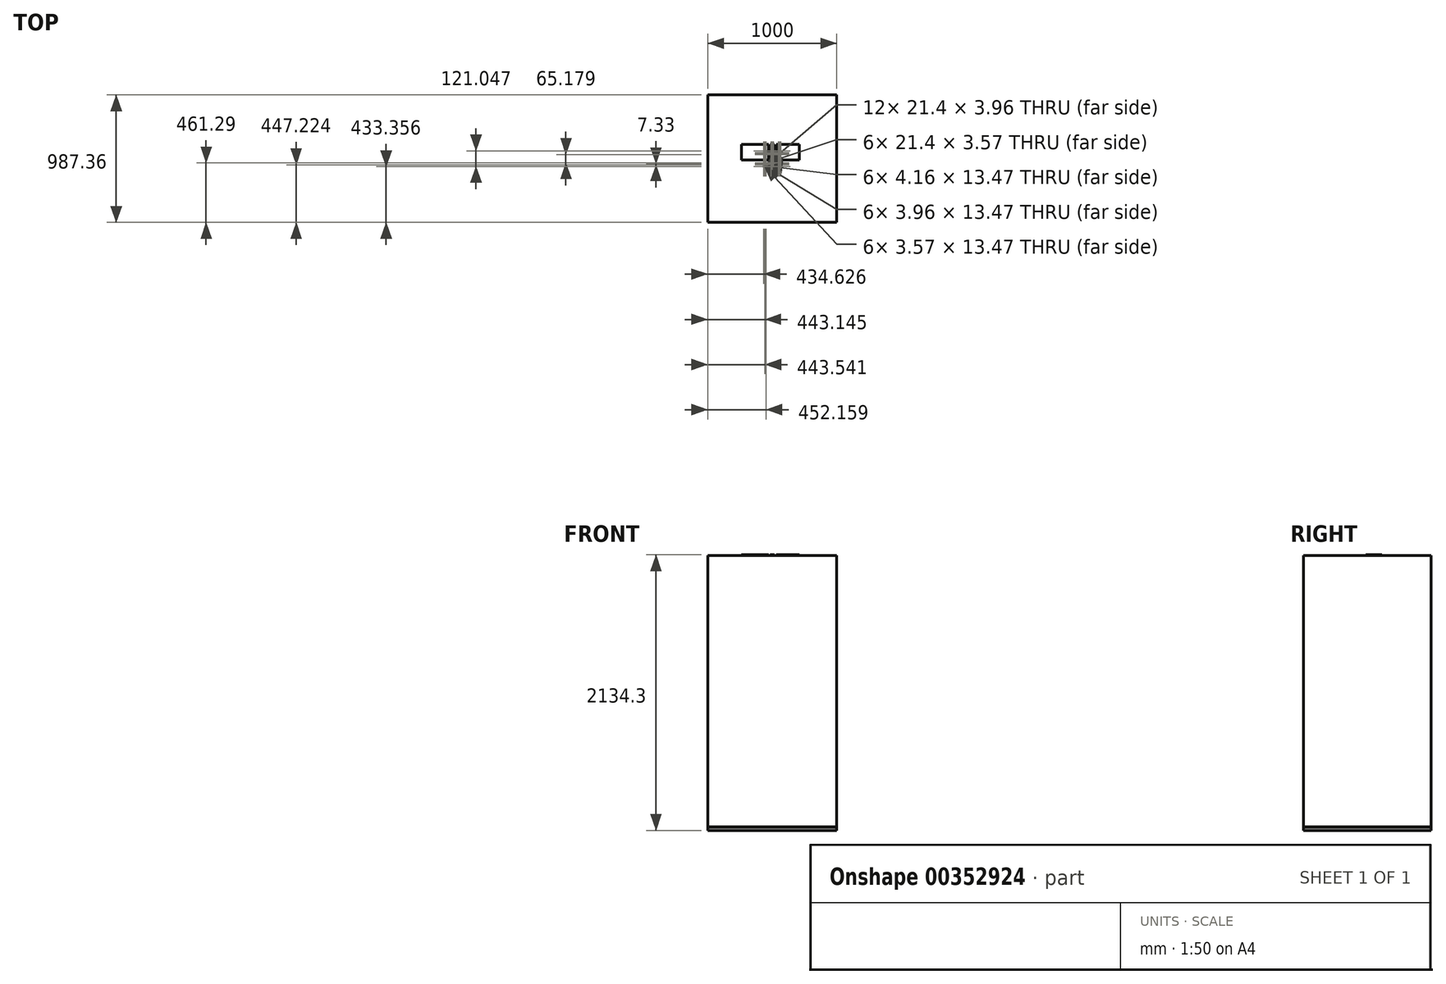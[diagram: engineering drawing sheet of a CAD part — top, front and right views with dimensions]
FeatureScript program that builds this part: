
annotation { "Feature Type Name" : "Feature", "Feature Type Description" : "" }
export const myFeature = defineFeature(function(context is Context, id is Id, definition is map)
    precondition{}
    {
        {
            var Q0;
            Q0=qCreatedBy(makeId("Top.planeOp"),FACE);
            var sketch = newSketch(context, id + "F0", { "sketchPlane" : qUnion([Q0])});
            skLineSegment(sketch, "E0.bottom", {"start": v(-500.4, 493.48) * mm, "end": v(499.6, 493.48) * mm});
            skLineSegment(sketch, "E0.top", {"start": v(-500.4, -493.88) * mm, "end": v(499.6, -493.88) * mm});
            skLineSegment(sketch, "E0.left", {"start": v(-500.4, 493.48) * mm, "end": v(-500.4, -493.88) * mm});
            skLineSegment(sketch, "E0.right", {"start": v(499.6, 493.48) * mm, "end": v(499.6, -493.88) * mm});
            skLineSegment(sketch, "E1.bottom", {"start": v(-441.4, 433.09) * mm, "end": v(443.42, 433.09) * mm});
            skLineSegment(sketch, "E1.top", {"start": v(-441.4, -436.3) * mm, "end": v(443.42, -436.3) * mm});
            skLineSegment(sketch, "E1.left", {"start": v(-441.4, 433.09) * mm, "end": v(-441.4, -436.3) * mm});
            skLineSegment(sketch, "E1.right", {"start": v(443.42, 433.09) * mm, "end": v(443.42, -436.3) * mm});
            skSolve(sketch);
        }
        {
            var Q0;
            Q0=makeQuery(id+"F0.imprint","IMPRINT",FACE,{"disambiguationData":[TD([[makeQuery(id+"F0.imprint","IMPRINT",EDGE,{"derivedFrom":sQuery(id+"F0.wireOp",EDGE,"E0.bottom")}),-1.0]])]});
            var Q1;
            Q1=makeQuery(id+"F0.imprint","IMPRINT",FACE,{"disambiguationData":[TD([[makeQuery(id+"F0.imprint","IMPRINT",EDGE,{"derivedFrom":sQuery(id+"F0.wireOp",EDGE,"E1.bottom")}),-1.0]])]});
            extrude(context, id + "F1", {"entities" : qUnion([Q0, Q1]), "depth" : 2100 * mm});
        }
        {
            var Q0;
            Q0=makeQuery(id+"F1.opExtrude","CAP_FACE",FACE,{"disambiguationData":[OSD([sQuery(id+"F0.wireOp",EDGE,"E0.bottom"),sQuery(id+"F0.wireOp",EDGE,"E0.top"),sQuery(id+"F0.wireOp",EDGE,"E0.left"),sQuery(id+"F0.wireOp",EDGE,"E0.right")])],"isStart":false});
            var sketch = newSketch(context, id + "F2", { "sketchPlane" : qUnion([Q0])});
            skLineSegment(sketch, "E2.bottom", {"start": v(-239.5, 111.47) * mm, "end": v(-29.32, 111.47) * mm});
            skLineSegment(sketch, "E2.top", {"start": v(-239.5, -10.2) * mm, "end": v(-29.32, -10.2) * mm});
            skLineSegment(sketch, "E2.left", {"start": v(-239.5, 111.47) * mm, "end": v(-239.5, -10.2) * mm});
            skLineSegment(sketch, "E2.right", {"start": v(-29.32, 111.47) * mm, "end": v(-29.32, -10.2) * mm});
            skLineSegment(sketch, "E3.bottom", {"start": v(-15.25, 111.47) * mm, "end": v(15.85, 111.47) * mm});
            skLineSegment(sketch, "E3.top", {"start": v(-15.25, -10.2) * mm, "end": v(15.85, -10.2) * mm});
            skLineSegment(sketch, "E3.left", {"start": v(-15.25, 111.47) * mm, "end": v(-15.25, -10.2) * mm});
            skLineSegment(sketch, "E3.right", {"start": v(15.85, 111.47) * mm, "end": v(15.85, -10.2) * mm});
            skLineSegment(sketch, "E4.bottom", {"start": v(30.7, 111.47) * mm, "end": v(210.08, 111.47) * mm});
            skLineSegment(sketch, "E4.top", {"start": v(30.7, -10.2) * mm, "end": v(210.08, -10.2) * mm});
            skLineSegment(sketch, "E4.left", {"start": v(30.7, 111.47) * mm, "end": v(30.7, -10.2) * mm});
            skLineSegment(sketch, "E4.right", {"start": v(210.08, 111.47) * mm, "end": v(210.08, -10.2) * mm});
            skSolve(sketch);
        }
        {
            var Q0;
            Q0=makeQuery(id+"F2.imprint","IMPRINT",FACE,{"disambiguationData":[TD([[makeQuery(id+"F2.imprint","IMPRINT",EDGE,{"derivedFrom":sQuery(id+"F2.wireOp",EDGE,"E3.bottom")}),-1.0]])]});
            var Q1;
            Q1=makeQuery(id+"F2.imprint","IMPRINT",FACE,{"disambiguationData":[TD([[makeQuery(id+"F2.imprint","IMPRINT",EDGE,{"derivedFrom":sQuery(id+"F2.wireOp",EDGE,"E4.bottom")}),-1.0]])]});
            var Q2;
            Q2=makeQuery(id+"F2.imprint","IMPRINT",FACE,{"disambiguationData":[TD([[makeQuery(id+"F2.imprint","IMPRINT",EDGE,{"derivedFrom":sQuery(id+"F2.wireOp",EDGE,"E2.bottom")}),-1.0]])]});
            extrude(context, id + "F3", {"entities" : qUnion([Q0, Q1, Q2]), "operationType" : NewBodyOperationType.ADD, "depth" : 5.8 * mm});
        }
        {
            var Q0;
            Q0=makeQuery(id+"F1.opExtrude","CAP_FACE",FACE,{"disambiguationData":[OSD([sQuery(id+"F0.wireOp",EDGE,"E0.bottom"),sQuery(id+"F0.wireOp",EDGE,"E0.top"),sQuery(id+"F0.wireOp",EDGE,"E0.left"),sQuery(id+"F0.wireOp",EDGE,"E0.right")])],"isStart":true});
            var sketch = newSketch(context, id + "F4", { "sketchPlane" : qUnion([Q0])});
            skLineSegment(sketch, "E5.bottom", {"start": v(-67.56, 67.26) * mm, "end": v(-64, 67.26) * mm});
            skLineSegment(sketch, "E5.top", {"start": v(-67.56, 53.79) * mm, "end": v(-64, 53.79) * mm});
            skLineSegment(sketch, "E5.left", {"start": v(-67.56, 67.26) * mm, "end": v(-67.56, 53.79) * mm});
            skLineSegment(sketch, "E5.right", {"start": v(-64, 67.26) * mm, "end": v(-64, 53.79) * mm});
            skLineSegment(sketch, "E6.bottom", {"start": v(-59.24, 67.26) * mm, "end": v(-55.27, 67.26) * mm});
            skLineSegment(sketch, "E6.top", {"start": v(-59.24, 53.79) * mm, "end": v(-55.27, 53.79) * mm});
            skLineSegment(sketch, "E6.left", {"start": v(-59.24, 67.26) * mm, "end": v(-59.24, 53.79) * mm});
            skLineSegment(sketch, "E6.right", {"start": v(-55.27, 67.26) * mm, "end": v(-55.27, 53.79) * mm});
            skLineSegment(sketch, "E7.bottom", {"start": v(-50.32, 67.26) * mm, "end": v(-46.16, 67.26) * mm});
            skLineSegment(sketch, "E7.top", {"start": v(-50.32, 53.79) * mm, "end": v(-46.16, 53.79) * mm});
            skLineSegment(sketch, "E7.left", {"start": v(-50.32, 67.26) * mm, "end": v(-50.32, 53.79) * mm});
            skLineSegment(sketch, "E7.right", {"start": v(-46.16, 67.26) * mm, "end": v(-46.16, 53.79) * mm});
            skLineSegment(sketch, "E8.1.0.0", {"start": v(-7.23, 66.87) * mm, "end": v(-7.23, 53.4) * mm});
            skLineSegment(sketch, "E8.1.0.1", {"start": v(1.48, 66.87) * mm, "end": v(1.48, 53.4) * mm});
            skLineSegment(sketch, "E8.1.0.2", {"start": v(-2.48, 66.87) * mm, "end": v(-2.48, 53.4) * mm});
            skLineSegment(sketch, "E8.1.0.3", {"start": v(6.44, 66.87) * mm, "end": v(6.44, 53.4) * mm});
            skLineSegment(sketch, "E8.1.0.4", {"start": v(10.6, 66.87) * mm, "end": v(10.6, 53.4) * mm});
            skLineSegment(sketch, "E8.1.0.5", {"start": v(-10.8, 66.87) * mm, "end": v(-7.23, 66.87) * mm});
            skLineSegment(sketch, "E8.1.0.6", {"start": v(-10.8, 53.4) * mm, "end": v(-7.23, 53.4) * mm});
            skLineSegment(sketch, "E8.1.0.7", {"start": v(-10.8, 66.87) * mm, "end": v(-10.8, 53.4) * mm});
            skLineSegment(sketch, "E8.1.0.8", {"start": v(-2.48, 66.87) * mm, "end": v(1.48, 66.87) * mm});
            skLineSegment(sketch, "E8.1.0.9", {"start": v(6.44, 66.87) * mm, "end": v(10.6, 66.87) * mm});
            skLineSegment(sketch, "E8.1.0.10", {"start": v(-2.48, 53.4) * mm, "end": v(1.48, 53.4) * mm});
            skLineSegment(sketch, "E8.1.0.11", {"start": v(6.44, 53.4) * mm, "end": v(10.6, 53.4) * mm});
            skLineSegment(sketch, "E8.2.0.0", {"start": v(49.52, 66.48) * mm, "end": v(49.52, 53.01) * mm});
            skLineSegment(sketch, "E8.2.0.1", {"start": v(58.24, 66.48) * mm, "end": v(58.24, 53.01) * mm});
            skLineSegment(sketch, "E8.2.0.2", {"start": v(54.28, 66.48) * mm, "end": v(54.28, 53.01) * mm});
            skLineSegment(sketch, "E8.2.0.3", {"start": v(63.2, 66.48) * mm, "end": v(63.2, 53.01) * mm});
            skLineSegment(sketch, "E8.2.0.4", {"start": v(67.35, 66.48) * mm, "end": v(67.35, 53.01) * mm});
            skLineSegment(sketch, "E8.2.0.5", {"start": v(45.96, 66.48) * mm, "end": v(49.52, 66.48) * mm});
            skLineSegment(sketch, "E8.2.0.6", {"start": v(45.96, 53.01) * mm, "end": v(49.52, 53.01) * mm});
            skLineSegment(sketch, "E8.2.0.7", {"start": v(45.96, 66.48) * mm, "end": v(45.96, 53.01) * mm});
            skLineSegment(sketch, "E8.2.0.8", {"start": v(54.28, 66.48) * mm, "end": v(58.24, 66.48) * mm});
            skLineSegment(sketch, "E8.2.0.9", {"start": v(63.2, 66.48) * mm, "end": v(67.35, 66.48) * mm});
            skLineSegment(sketch, "E8.2.0.10", {"start": v(54.28, 53.01) * mm, "end": v(58.24, 53.01) * mm});
            skLineSegment(sketch, "E8.2.0.11", {"start": v(63.2, 53.01) * mm, "end": v(67.35, 53.01) * mm});
            skLineSegment(sketch, "E9.MirrorCS", {"start": v(-59.24, -53.79) * mm, "end": v(-55.27, -53.79) * mm});
            skLineSegment(sketch, "E10.MirrorCS", {"start": v(-67.56, -53.79) * mm, "end": v(-64, -53.79) * mm});
            skLineSegment(sketch, "E11.MirrorCS", {"start": v(-50.32, -53.79) * mm, "end": v(-46.16, -53.79) * mm});
            skLineSegment(sketch, "E12.MirrorCS", {"start": v(54.28, -53.01) * mm, "end": v(58.24, -53.01) * mm});
            skLineSegment(sketch, "E13.MirrorCS", {"start": v(-10.8, -66.87) * mm, "end": v(-7.23, -66.87) * mm});
            skLineSegment(sketch, "E14.MirrorCS", {"start": v(-50.32, -67.26) * mm, "end": v(-46.16, -67.26) * mm});
            skLineSegment(sketch, "E15.MirrorCS", {"start": v(-10.8, -53.4) * mm, "end": v(-7.23, -53.4) * mm});
            skLineSegment(sketch, "E16.MirrorCS", {"start": v(54.28, -66.48) * mm, "end": v(58.24, -66.48) * mm});
            skLineSegment(sketch, "E17.MirrorCS", {"start": v(-67.56, -67.26) * mm, "end": v(-64, -67.26) * mm});
            skLineSegment(sketch, "E18.MirrorCS", {"start": v(-59.24, -67.26) * mm, "end": v(-55.27, -67.26) * mm});
            skLineSegment(sketch, "E19.MirrorCS", {"start": v(45.96, -53.01) * mm, "end": v(49.52, -53.01) * mm});
            skLineSegment(sketch, "E20.MirrorCS", {"start": v(6.44, -66.87) * mm, "end": v(10.6, -66.87) * mm});
            skLineSegment(sketch, "E21.MirrorCS", {"start": v(45.96, -66.48) * mm, "end": v(49.52, -66.48) * mm});
            skLineSegment(sketch, "E22.MirrorCS", {"start": v(-2.48, -66.87) * mm, "end": v(1.48, -66.87) * mm});
            skLineSegment(sketch, "E23.MirrorCS", {"start": v(-2.48, -53.4) * mm, "end": v(1.48, -53.4) * mm});
            skLineSegment(sketch, "E24.MirrorCS", {"start": v(6.44, -53.4) * mm, "end": v(10.6, -53.4) * mm});
            skLineSegment(sketch, "E25.MirrorCS", {"start": v(58.24, -66.48) * mm, "end": v(58.24, -53.01) * mm});
            skLineSegment(sketch, "E26.MirrorCS", {"start": v(-2.48, -66.87) * mm, "end": v(-2.48, -53.4) * mm});
            skLineSegment(sketch, "E27.MirrorCS", {"start": v(1.48, -66.87) * mm, "end": v(1.48, -53.4) * mm});
            skLineSegment(sketch, "E28.MirrorCS", {"start": v(67.35, -66.48) * mm, "end": v(67.35, -53.01) * mm});
            skLineSegment(sketch, "E29.MirrorCS", {"start": v(54.28, -66.48) * mm, "end": v(54.28, -53.01) * mm});
            skLineSegment(sketch, "E30.MirrorCS", {"start": v(63.2, -66.48) * mm, "end": v(63.2, -53.01) * mm});
            skLineSegment(sketch, "E31.MirrorCS", {"start": v(10.6, -66.87) * mm, "end": v(10.6, -53.4) * mm});
            skLineSegment(sketch, "E32.MirrorCS", {"start": v(-59.24, -67.26) * mm, "end": v(-59.24, -53.79) * mm});
            skLineSegment(sketch, "E33.MirrorCS", {"start": v(-55.27, -67.26) * mm, "end": v(-55.27, -53.79) * mm});
            skLineSegment(sketch, "E34.MirrorCS", {"start": v(45.96, -66.48) * mm, "end": v(45.96, -53.01) * mm});
            skLineSegment(sketch, "E35.MirrorCS", {"start": v(6.44, -66.87) * mm, "end": v(6.44, -53.4) * mm});
            skLineSegment(sketch, "E36.MirrorCS", {"start": v(-64, -67.26) * mm, "end": v(-64, -53.79) * mm});
            skLineSegment(sketch, "E37.MirrorCS", {"start": v(-67.56, -67.26) * mm, "end": v(-67.56, -53.79) * mm});
            skLineSegment(sketch, "E38.MirrorCS", {"start": v(-46.16, -67.26) * mm, "end": v(-46.16, -53.79) * mm});
            skLineSegment(sketch, "E39.MirrorCS", {"start": v(-50.32, -67.26) * mm, "end": v(-50.32, -53.79) * mm});
            skLineSegment(sketch, "E40.MirrorCS", {"start": v(63.2, -66.48) * mm, "end": v(67.35, -66.48) * mm});
            skLineSegment(sketch, "E41.MirrorCS", {"start": v(-10.8, -66.87) * mm, "end": v(-10.8, -53.4) * mm});
            skLineSegment(sketch, "E42.MirrorCS", {"start": v(63.2, -53.01) * mm, "end": v(67.35, -53.01) * mm});
            skLineSegment(sketch, "E43.MirrorCS", {"start": v(-7.23, -66.87) * mm, "end": v(-7.23, -53.4) * mm});
            skLineSegment(sketch, "E44.MirrorCS", {"start": v(49.52, -66.48) * mm, "end": v(49.52, -53.01) * mm});
            skLineSegment(sketch, "E45.bottom", {"start": v(-67.56, 48.64) * mm, "end": v(-46.16, 48.64) * mm});
            skLineSegment(sketch, "E45.top", {"start": v(-67.56, 44.67) * mm, "end": v(-46.16, 44.67) * mm});
            skLineSegment(sketch, "E45.left", {"start": v(-67.56, 48.64) * mm, "end": v(-67.56, 44.67) * mm});
            skLineSegment(sketch, "E45.right", {"start": v(-46.16, 48.64) * mm, "end": v(-46.16, 44.67) * mm});
            skLineSegment(sketch, "E46.bottom", {"start": v(-67.56, 41.3) * mm, "end": v(-46.16, 41.3) * mm});
            skLineSegment(sketch, "E46.top", {"start": v(-67.56, 37.34) * mm, "end": v(-46.16, 37.34) * mm});
            skLineSegment(sketch, "E46.left", {"start": v(-67.56, 41.3) * mm, "end": v(-67.56, 37.34) * mm});
            skLineSegment(sketch, "E46.right", {"start": v(-46.16, 41.3) * mm, "end": v(-46.16, 37.34) * mm});
            skLineSegment(sketch, "E47.bottom", {"start": v(-67.56, 34.37) * mm, "end": v(-46.16, 34.37) * mm});
            skLineSegment(sketch, "E47.top", {"start": v(-67.56, 30.8) * mm, "end": v(-46.16, 30.8) * mm});
            skLineSegment(sketch, "E47.left", {"start": v(-67.56, 34.37) * mm, "end": v(-67.56, 30.8) * mm});
            skLineSegment(sketch, "E47.right", {"start": v(-46.16, 34.37) * mm, "end": v(-46.16, 30.8) * mm});
            skLineSegment(sketch, "E48.1.0.0", {"start": v(-10.9, 37.34) * mm, "end": v(10.5, 37.34) * mm});
            skLineSegment(sketch, "E48.1.0.1", {"start": v(-10.9, 48.63) * mm, "end": v(10.5, 48.63) * mm});
            skLineSegment(sketch, "E48.1.0.2", {"start": v(-10.9, 41.3) * mm, "end": v(10.5, 41.3) * mm});
            skLineSegment(sketch, "E48.1.0.3", {"start": v(-10.9, 30.8) * mm, "end": v(10.5, 30.8) * mm});
            skLineSegment(sketch, "E48.1.0.4", {"start": v(-10.9, 34.37) * mm, "end": v(10.5, 34.37) * mm});
            skLineSegment(sketch, "E48.1.0.5", {"start": v(-10.9, 44.67) * mm, "end": v(10.5, 44.67) * mm});
            skLineSegment(sketch, "E48.1.0.6", {"start": v(-10.9, 34.37) * mm, "end": v(-10.9, 30.8) * mm});
            skLineSegment(sketch, "E48.1.0.7", {"start": v(10.5, 41.3) * mm, "end": v(10.5, 37.34) * mm});
            skLineSegment(sketch, "E48.1.0.8", {"start": v(-10.9, 41.3) * mm, "end": v(-10.9, 37.34) * mm});
            skLineSegment(sketch, "E48.1.0.9", {"start": v(10.5, 48.63) * mm, "end": v(10.5, 44.67) * mm});
            skLineSegment(sketch, "E48.1.0.10", {"start": v(-10.9, 48.63) * mm, "end": v(-10.9, 44.67) * mm});
            skLineSegment(sketch, "E48.1.0.11", {"start": v(10.5, 34.37) * mm, "end": v(10.5, 30.8) * mm});
            skLineSegment(sketch, "E48.2.0.0", {"start": v(45.76, 37.33) * mm, "end": v(67.15, 37.33) * mm});
            skLineSegment(sketch, "E48.2.0.1", {"start": v(45.76, 48.62) * mm, "end": v(67.15, 48.62) * mm});
            skLineSegment(sketch, "E48.2.0.2", {"start": v(45.76, 41.3) * mm, "end": v(67.15, 41.3) * mm});
            skLineSegment(sketch, "E48.2.0.3", {"start": v(45.76, 30.8) * mm, "end": v(67.15, 30.8) * mm});
            skLineSegment(sketch, "E48.2.0.4", {"start": v(45.76, 34.36) * mm, "end": v(67.15, 34.36) * mm});
            skLineSegment(sketch, "E48.2.0.5", {"start": v(45.76, 44.66) * mm, "end": v(67.15, 44.66) * mm});
            skLineSegment(sketch, "E48.2.0.6", {"start": v(45.76, 34.36) * mm, "end": v(45.76, 30.8) * mm});
            skLineSegment(sketch, "E48.2.0.7", {"start": v(67.15, 41.3) * mm, "end": v(67.15, 37.33) * mm});
            skLineSegment(sketch, "E48.2.0.8", {"start": v(45.76, 41.3) * mm, "end": v(45.76, 37.33) * mm});
            skLineSegment(sketch, "E48.2.0.9", {"start": v(67.15, 48.62) * mm, "end": v(67.15, 44.66) * mm});
            skLineSegment(sketch, "E48.2.0.10", {"start": v(45.76, 48.62) * mm, "end": v(45.76, 44.66) * mm});
            skLineSegment(sketch, "E48.2.0.11", {"start": v(67.15, 34.36) * mm, "end": v(67.15, 30.8) * mm});
            skLineSegment(sketch, "E49.MirrorCS", {"start": v(67.15, -48.62) * mm, "end": v(67.15, -44.66) * mm});
            skLineSegment(sketch, "E50.MirrorCS", {"start": v(10.5, -48.63) * mm, "end": v(10.5, -44.67) * mm});
            skLineSegment(sketch, "E51.MirrorCS", {"start": v(-10.9, -34.37) * mm, "end": v(-10.9, -30.8) * mm});
            skLineSegment(sketch, "E52.MirrorCS", {"start": v(-67.56, -48.64) * mm, "end": v(-67.56, -44.67) * mm});
            skLineSegment(sketch, "E53.MirrorCS", {"start": v(67.15, -41.3) * mm, "end": v(67.15, -37.33) * mm});
            skLineSegment(sketch, "E54.MirrorCS", {"start": v(-10.9, -41.3) * mm, "end": v(-10.9, -37.34) * mm});
            skLineSegment(sketch, "E55.MirrorCS", {"start": v(-10.9, -48.63) * mm, "end": v(-10.9, -44.67) * mm});
            skLineSegment(sketch, "E56.MirrorCS", {"start": v(-67.56, -41.3) * mm, "end": v(-67.56, -37.34) * mm});
            skLineSegment(sketch, "E57.MirrorCS", {"start": v(-46.16, -34.37) * mm, "end": v(-46.16, -30.8) * mm});
            skLineSegment(sketch, "E58.MirrorCS", {"start": v(10.5, -34.37) * mm, "end": v(10.5, -30.8) * mm});
            skLineSegment(sketch, "E59.MirrorCS", {"start": v(-46.16, -48.64) * mm, "end": v(-46.16, -44.67) * mm});
            skLineSegment(sketch, "E60.MirrorCS", {"start": v(-46.16, -41.3) * mm, "end": v(-46.16, -37.34) * mm});
            skLineSegment(sketch, "E61.MirrorCS", {"start": v(67.15, -34.36) * mm, "end": v(67.15, -30.8) * mm});
            skLineSegment(sketch, "E62.MirrorCS", {"start": v(10.5, -41.3) * mm, "end": v(10.5, -37.34) * mm});
            skLineSegment(sketch, "E63.MirrorCS", {"start": v(45.76, -48.62) * mm, "end": v(45.76, -44.66) * mm});
            skLineSegment(sketch, "E64.MirrorCS", {"start": v(-67.56, -34.37) * mm, "end": v(-67.56, -30.8) * mm});
            skLineSegment(sketch, "E65.MirrorCS", {"start": v(45.76, -34.36) * mm, "end": v(45.76, -30.8) * mm});
            skLineSegment(sketch, "E66.MirrorCS", {"start": v(45.76, -41.3) * mm, "end": v(45.76, -37.33) * mm});
            skLineSegment(sketch, "E67.MirrorCS", {"start": v(-10.9, -44.67) * mm, "end": v(10.5, -44.67) * mm});
            skLineSegment(sketch, "E68.MirrorCS", {"start": v(45.76, -30.8) * mm, "end": v(67.15, -30.8) * mm});
            skLineSegment(sketch, "E69.MirrorCS", {"start": v(-67.56, -37.34) * mm, "end": v(-46.16, -37.34) * mm});
            skLineSegment(sketch, "E70.MirrorCS", {"start": v(-67.56, -30.8) * mm, "end": v(-46.16, -30.8) * mm});
            skLineSegment(sketch, "E71.MirrorCS", {"start": v(-67.56, -44.67) * mm, "end": v(-46.16, -44.67) * mm});
            skLineSegment(sketch, "E72.MirrorCS", {"start": v(-67.56, -34.37) * mm, "end": v(-46.16, -34.37) * mm});
            skLineSegment(sketch, "E73.MirrorCS", {"start": v(45.76, -34.36) * mm, "end": v(67.15, -34.36) * mm});
            skLineSegment(sketch, "E74.MirrorCS", {"start": v(-10.9, -30.8) * mm, "end": v(10.5, -30.8) * mm});
            skLineSegment(sketch, "E75.MirrorCS", {"start": v(-10.9, -48.63) * mm, "end": v(10.5, -48.63) * mm});
            skLineSegment(sketch, "E76.MirrorCS", {"start": v(45.76, -37.33) * mm, "end": v(67.15, -37.33) * mm});
            skLineSegment(sketch, "E77.MirrorCS", {"start": v(45.76, -44.66) * mm, "end": v(67.15, -44.66) * mm});
            skLineSegment(sketch, "E78.MirrorCS", {"start": v(-67.56, -41.3) * mm, "end": v(-46.16, -41.3) * mm});
            skLineSegment(sketch, "E79.MirrorCS", {"start": v(-10.9, -41.3) * mm, "end": v(10.5, -41.3) * mm});
            skLineSegment(sketch, "E80.MirrorCS", {"start": v(-10.9, -37.34) * mm, "end": v(10.5, -37.34) * mm});
            skLineSegment(sketch, "E81.MirrorCS", {"start": v(45.76, -48.62) * mm, "end": v(67.15, -48.62) * mm});
            skLineSegment(sketch, "E82.MirrorCS", {"start": v(45.76, -41.3) * mm, "end": v(67.15, -41.3) * mm});
            skLineSegment(sketch, "E83.MirrorCS", {"start": v(-67.56, -48.64) * mm, "end": v(-46.16, -48.64) * mm});
            skLineSegment(sketch, "E84.MirrorCS", {"start": v(-10.9, -34.37) * mm, "end": v(10.5, -34.37) * mm});
            skSolve(sketch);
        }
        {
            var Q0;
            Q0 = qSketchRegion(id + "F4", true);
            extrude(context, id + "F5", {"entities" : qUnion([Q0]), "operationType" : NewBodyOperationType.ADD, "depth" : 3.5 * mm});
        }
        {
            var Q0;
            Q0=makeQuery(id+"F5.opExtrude","CAP_FACE",FACE,{"disambiguationData":[OSD([sQuery(id+"F4.wireOp",EDGE,"E5.bottom"),sQuery(id+"F4.wireOp",EDGE,"E5.top"),sQuery(id+"F4.wireOp",EDGE,"E5.left"),sQuery(id+"F4.wireOp",EDGE,"E5.right")])],"isStart":false});
            var sketch = newSketch(context, id + "F6", { "sketchPlane" : qUnion([Q0])});
            skLineSegment(sketch, "E85.0", {"start": v(-500.4, 493.88) * mm, "end": v(499.6, 493.88) * mm});
            skLineSegment(sketch, "E86.0", {"start": v(-500.4, -493.48) * mm, "end": v(-500.4, 493.88) * mm});
            skLineSegment(sketch, "E87.0", {"start": v(-500.4, -493.48) * mm, "end": v(499.6, -493.48) * mm});
            skLineSegment(sketch, "E88.0", {"start": v(499.6, -493.48) * mm, "end": v(499.6, 493.88) * mm});
            skSolve(sketch);
        }
        {
            var Q0;
            Q0=makeQuery(id+"F6.imprint","IMPRINT",FACE,{"disambiguationData":[TD([[makeQuery(id+"F6.imprint","IMPRINT",EDGE,{"derivedFrom":sQuery(id+"F6.wireOp",EDGE,"E85.0")}),-1.0]])]});
            var Q1;
            Q1=makeQuery(id+"F6.imprint","IMPRINT",FACE,{"disambiguationData":[TD([[makeQuery(id+"F6.imprint","IMPRINT",EDGE,{"derivedFrom":makeQuery(id+"F5.opExtrude","CAP_EDGE",EDGE,{"disambiguationData":[OSD([sQuery(id+"F4.wireOp",EDGE,"E5.bottom")])],"isStart":false})}),-1.0]])]});
            extrude(context, id + "F7", {"entities" : qUnion([Q0, Q1]), "operationType" : NewBodyOperationType.ADD, "depth" : 25 * mm});
        }
    });
